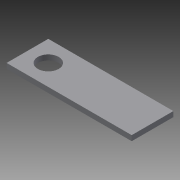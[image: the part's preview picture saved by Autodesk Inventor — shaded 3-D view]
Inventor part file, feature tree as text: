
AUTODESK INVENTOR PART (.ipt)
format: ipt  version: 2013 (Build 170138000, 138)  size: 101,376 bytes
history: native  units: in
note: dims shown in document units (in); Inventor stores cm internally (conversion verified against a paired STEP export)
features: extrude x5, sketch x5
ambient origin geometry x8: Origin, YZ Plane, XZ Plane, XY Plane, X Axis, Y Axis, Z Axis, Center Point
bodies: Solid1 (feature_tree)
feature tree (10):
  extrude  "Extrusion1"  Depth=1.0in
  extrude  "Extrusion2"  TaperAngle=0.0deg  [1 undecoded]
  extrude  "Extrusion3"  TaperAngle=180.0deg  [1 undecoded]
  extrude  "Extrusion4"  Depth=0.25in
  extrude  "Extrusion5"  Depth=0.125in TaperAngle=0.0deg
  sketch  "Sketch1"  dims[d0=6.0in d1=1.0in]
  sketch  "Sketch2"  dims[d2=0.5in d3=0.0in]
  sketch  "Sketch3"  dims[d4=1.0in d5=180.0deg]
  sketch  "Sketch4"  dims[d6=1.0in d7=0.25in]
  sketch  "Sketch5"  dims[d8=0.25in d9=0.125in d10=0.0in d11=0.25in d12=1.0in d13=0.0in d14=0.5in d15=1.0in d16=0.0in d17=1.0in d18=0.0in d19=0.125in d20=0.0in]
note: 2 required parameter values undecoded (feature->parameter linkage not recoverable at this tier; creation-order binding heuristic only, values carry confidence <= 0.55)
